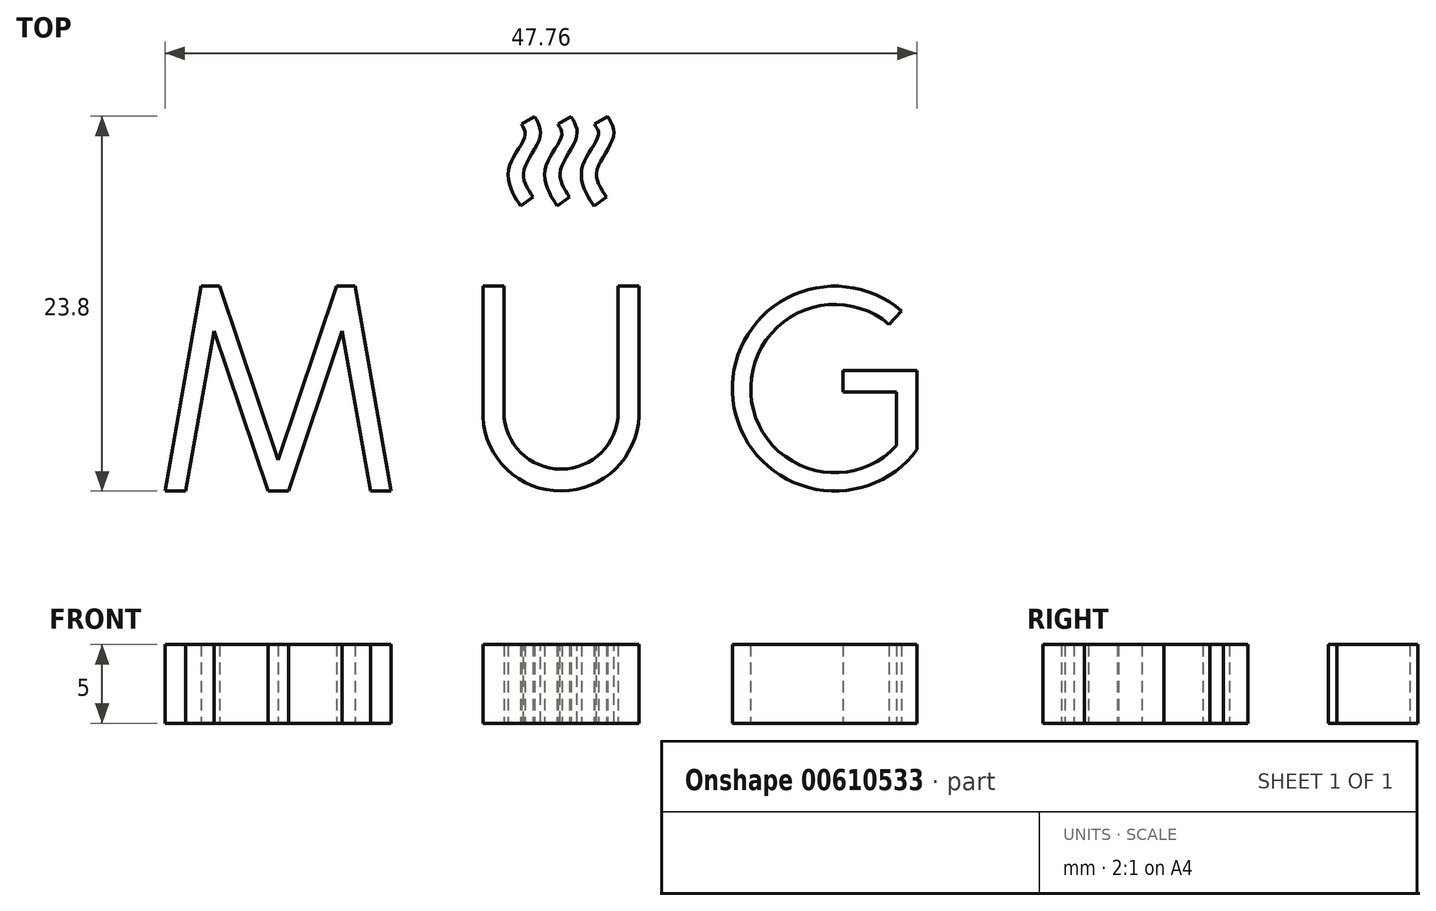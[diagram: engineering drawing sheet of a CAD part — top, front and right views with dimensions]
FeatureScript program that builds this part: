
annotation { "Feature Type Name" : "Feature", "Feature Type Description" : "" }
export const myFeature = defineFeature(function(context is Context, id is Id, definition is map)
    precondition{}
    {
        {
            var Q0;
            Q0=qCreatedBy(makeId("Top.planeOp"),FACE);
            var sketch = newSketch(context, id + "F0", { "sketchPlane" : qUnion([Q0]), "disableImprinting" : false});
            skLineSegment(sketch, "E0", {"start": v(-22.74, 7.47) * mm, "end": v(-25.03, -5.54) * mm});
            skLineSegment(sketch, "E1", {"start": v(-25.03, -5.54) * mm, "end": v(-23.72, -5.54) * mm});
            skLineSegment(sketch, "E2", {"start": v(-21.93, 4.61) * mm, "end": v(-23.72, -5.54) * mm});
            skLineSegment(sketch, "E3", {"start": v(-21.93, 4.61) * mm, "end": v(-18.5, -5.54) * mm});
            skLineSegment(sketch, "E4", {"start": v(-18.5, -5.54) * mm, "end": v(-17.2, -5.54) * mm});
            skLineSegment(sketch, "E5", {"start": v(-17.2, -5.54) * mm, "end": v(-13.78, 4.61) * mm});
            skLineSegment(sketch, "E6", {"start": v(-13.78, 4.61) * mm, "end": v(-11.99, -5.54) * mm});
            skLineSegment(sketch, "E7", {"start": v(-11.99, -5.54) * mm, "end": v(-10.67, -5.54) * mm});
            skLineSegment(sketch, "E8", {"start": v(-10.67, -5.54) * mm, "end": v(-12.97, 7.47) * mm});
            skLineSegment(sketch, "E9", {"start": v(-12.97, 7.47) * mm, "end": v(-14.13, 7.47) * mm});
            skLineSegment(sketch, "E10", {"start": v(-14.13, 7.47) * mm, "end": v(-17.85, -3.58) * mm});
            skLineSegment(sketch, "E11", {"start": v(-17.85, -3.58) * mm, "end": v(-21.58, 7.47) * mm});
            skLineSegment(sketch, "E12", {"start": v(-21.58, 7.47) * mm, "end": v(-22.74, 7.47) * mm});
            skLineSegment(sketch, "E13", {"start": v(-4.85, 7.47) * mm, "end": v(-3.52, 7.47) * mm});
            skArc(sketch, "E14", {"start": v(-3.52, -0.53) * mm, "mid": v(0.11, -4.15) * mm, "end": v(3.74, -0.53) * mm});
            skLineSegment(sketch, "E15", {"start": v(-3.52, 7.47) * mm, "end": v(-3.52, -0.53) * mm});
            skLineSegment(sketch, "E16", {"start": v(3.74, 7.47) * mm, "end": v(3.74, -0.53) * mm});
            skLineSegment(sketch, "E17", {"start": v(3.74, 7.47) * mm, "end": v(5.07, 7.47) * mm});
            skLineSegment(sketch, "E18", {"start": v(5.07, 7.47) * mm, "end": v(5.07, -0.76) * mm});
            skLineSegment(sketch, "E19", {"start": v(-4.85, 7.47) * mm, "end": v(-4.85, -0.82) * mm});
            skArc(sketch, "E20", {"start": v(-4.85, -0.82) * mm, "mid": v(0.13, -5.54) * mm, "end": v(5.07, -0.76) * mm});
            skArc(sketch, "E21", {"start": v(20.95, 5.05) * mm, "mid": v(12.17, 0.63) * mm, "end": v(21.43, -2.66) * mm});
            skArc(sketch, "E22", {"start": v(21.74, 5.9) * mm, "mid": v(11.04, 0.23) * mm, "end": v(22.73, -2.9) * mm});
            skPoint(sketch, "E23.0", {"position": v(12.16, 1.13) * mm});
            skPoint(sketch, "E24.0", {"position": v(11, 1.34) * mm});
            skLineSegment(sketch, "E25", {"start": v(21.74, 5.9) * mm, "end": v(20.95, 5.05) * mm});
            skLineSegment(sketch, "E26", {"start": v(21.43, -2.66) * mm, "end": v(21.43, 0.73) * mm});
            skLineSegment(sketch, "E27", {"start": v(21.43, 0.73) * mm, "end": v(18.01, 0.73) * mm});
            skLineSegment(sketch, "E28", {"start": v(18.01, 0.73) * mm, "end": v(18.01, 2.12) * mm});
            skLineSegment(sketch, "E29", {"start": v(18.01, 2.12) * mm, "end": v(22.73, 2.12) * mm});
            skLineSegment(sketch, "E30", {"start": v(22.73, 2.12) * mm, "end": v(22.73, -2.9) * mm});
            skFitSpline(sketch, "E31", {"points": [v(-2.4, 17.75) * mm, v(-2.15, 17.16) * mm, v(-3.22, 14.85) * mm, v(-2.45, 12.57) * mm], "startDerivative": vector(0.3, -0.78) * mm, "endDerivative": vector(2.56, -3.3) * mm});
            skFitSpline(sketch, "E32", {"points": [v(-0.08, 17.75) * mm, v(0.17, 17.16) * mm, v(-0.9, 14.85) * mm, v(-0.13, 12.57) * mm], "startDerivative": vector(0.31, -0.85) * mm, "endDerivative": vector(2.56, -3.3) * mm});
            skFitSpline(sketch, "E33", {"points": [v(2.24, 17.75) * mm, v(2.5, 17.16) * mm, v(1.42, 14.85) * mm, v(2.2, 12.57) * mm], "startDerivative": vector(0.27, -0.81) * mm, "endDerivative": vector(2.56, -3.3) * mm});
            skLineSegment(sketch, "E34", {"start": v(-0.08, 17.75) * mm, "end": v(0.75, 18.26) * mm});
            skLineSegment(sketch, "E35", {"start": v(2.24, 17.75) * mm, "end": v(3.07, 18.26) * mm});
            skLineSegment(sketch, "E36", {"start": v(-2.4, 17.75) * mm, "end": v(-1.58, 18.26) * mm});
            skLineSegment(sketch, "E37", {"start": v(-2.45, 12.57) * mm, "end": v(-1.66, 13.12) * mm});
            skLineSegment(sketch, "E38", {"start": v(-0.13, 12.57) * mm, "end": v(0.67, 13.12) * mm});
            skLineSegment(sketch, "E39", {"start": v(2.2, 12.57) * mm, "end": v(3, 13.12) * mm});
            skFitSpline(sketch, "E40", {"points": [v(3.07, 18.26) * mm, v(3.46, 17.2) * mm, v(2.39, 14.78) * mm, v(3, 13.12) * mm], "startDerivative": vector(0.5, -1.39) * mm, "endDerivative": vector(2.95, -4.8) * mm});
            skFitSpline(sketch, "E41", {"points": [v(0.75, 18.26) * mm, v(1.14, 17.2) * mm, v(0.06, 14.78) * mm, v(0.67, 13.12) * mm], "startDerivative": vector(0.5, -1.39) * mm, "endDerivative": vector(2.95, -4.8) * mm});
            skFitSpline(sketch, "E42", {"points": [v(-1.58, 18.26) * mm, v(-1.19, 17.2) * mm, v(-2.26, 14.78) * mm, v(-1.66, 13.12) * mm], "startDerivative": vector(0.5, -1.39) * mm, "endDerivative": vector(2.95, -4.8) * mm});
            skLineSegment(sketch, "E43", {"start": v(-28.72, -5.54) * mm, "end": v(25.68, -5.54) * mm, "construction": true});
            skLineSegment(sketch, "E44", {"start": v(-28.72, 7.47) * mm, "end": v(25.68, 7.47) * mm, "construction": true});
            skSolve(sketch);
        }
        {
            var Q0;
            Q0=makeQuery(id+"F0.imprint","IMPRINT",FACE,{"disambiguationData":[TD([[makeQuery(id+"F0.imprint","IMPRINT",EDGE,{"derivedFrom":sQuery(id+"F0.wireOp",EDGE,"E0")}),1.0]])]});
            var Q1;
            Q1=makeQuery(id+"F0.imprint","IMPRINT",FACE,{"disambiguationData":[TD([[makeQuery(id+"F0.imprint","IMPRINT",EDGE,{"derivedFrom":sQuery(id+"F0.wireOp",EDGE,"E13")}),-1.0]])]});
            var Q2;
            Q2=makeQuery(id+"F0.imprint","IMPRINT",FACE,{"disambiguationData":[TD([[makeQuery(id+"F0.imprint","IMPRINT",EDGE,{"derivedFrom":sQuery(id+"F0.wireOp",EDGE,"E21")}),-1.0]])]});
            var Q3;
            Q3=makeQuery(id+"F0.imprint","IMPRINT",FACE,{"disambiguationData":[TD([[makeQuery(id+"F0.imprint","IMPRINT",EDGE,{"derivedFrom":sQuery(id+"F0.wireOp",EDGE,"E33")}),1.0]])]});
            var Q4;
            Q4=makeQuery(id+"F0.imprint","IMPRINT",FACE,{"disambiguationData":[TD([[makeQuery(id+"F0.imprint","IMPRINT",EDGE,{"derivedFrom":sQuery(id+"F0.wireOp",EDGE,"E32")}),1.0]])]});
            var Q5;
            Q5=makeQuery(id+"F0.imprint","IMPRINT",FACE,{"disambiguationData":[TD([[makeQuery(id+"F0.imprint","IMPRINT",EDGE,{"derivedFrom":sQuery(id+"F0.wireOp",EDGE,"E31")}),1.0]])]});
            extrude(context, id + "F1", {"entities" : qUnion([Q0, Q1, Q2, Q3, Q4, Q5]), "depth" : 5 * mm, "offsetDistance" : 25 * mm});
        }
    });
